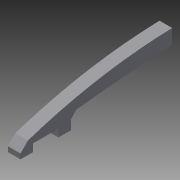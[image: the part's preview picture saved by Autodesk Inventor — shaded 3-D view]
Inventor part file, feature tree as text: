
AUTODESK INVENTOR PART (.ipt)
format: ipt  version: 2015 (Build 190159000, 159)  size: 109,056 bytes
history: native  units: mm
features: extrude x2, chamfer x2, sketch x2
ambient origin geometry x8: Origin, YZ Plane, XZ Plane, XY Plane, X Axis, Y Axis, Z Axis, Center Point
bodies: Body1 (feature_tree)
feature tree (6):
  extrude  "Extrusion3"  Depth=5.0mm
  extrude  "Extrusion4"  Depth=20.0mm
  chamfer  "Chamfer1"  Distance=5.0mm
  chamfer  "Chamfer2"  Distance=10.0mm
  sketch  "Sketch1"  dims[d0=20.0mm d9=5.0mm]
  sketch  "Sketch3"  dims[d11=40.0mm d13=20.0mm d14=5.0mm d16=10.0mm d17=3.0mm d19=6.0mm d20=40.0mm d21=200.0mm d22=400.0mm d24=12.0mm d25=5.0mm d26=0.0mm d27=10.0mm d28=5.0mm d29=3.0mm d30=0.0mm d32=2.0mm d33=2.0mm d34=45.0deg d35=3.0mm d36=2.0mm d37=45.0deg]
